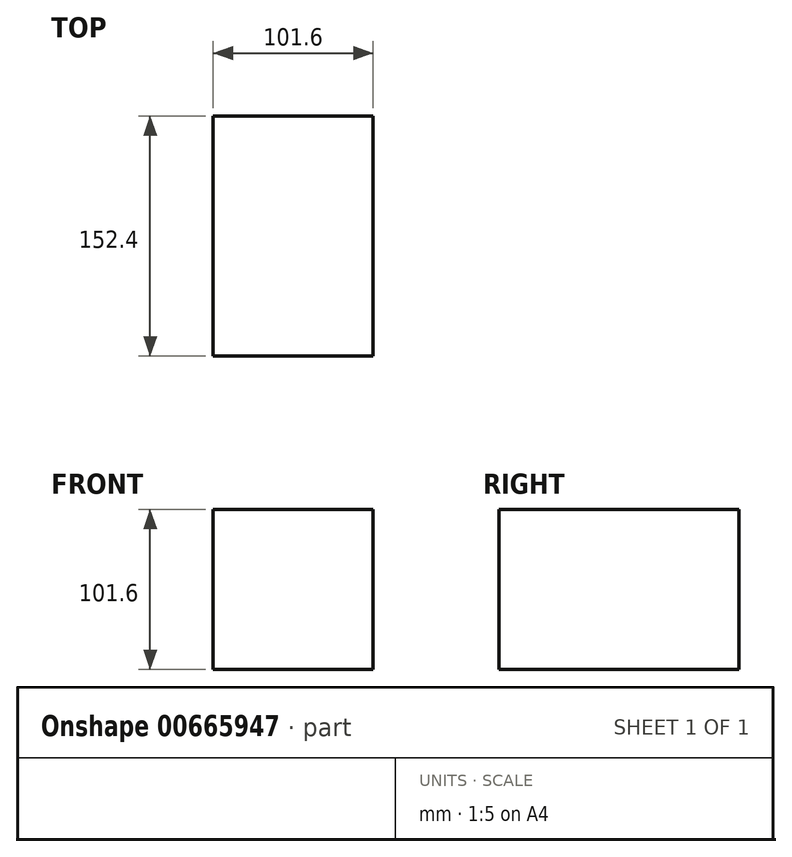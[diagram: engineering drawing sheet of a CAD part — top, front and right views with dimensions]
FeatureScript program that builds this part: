
annotation { "Feature Type Name" : "Feature", "Feature Type Description" : "" }
export const myFeature = defineFeature(function(context is Context, id is Id, definition is map)
    precondition{}
    {
        {
            var Q0;
            Q0=qCreatedBy(makeId("Top.planeOp"),FACE);
            var sketch = newSketch(context, id + "F0", { "sketchPlane" : qUnion([Q0])});
            skLineSegment(sketch, "E0", {"start": v(0, 0) * mm, "end": v(0, 152.4) * mm});
            skLineSegment(sketch, "E1", {"start": v(0, 152.4) * mm, "end": v(101.6, 152.4) * mm});
            skLineSegment(sketch, "E2", {"start": v(101.6, 152.4) * mm, "end": v(101.6, 0) * mm});
            skLineSegment(sketch, "E3", {"start": v(101.6, 0) * mm, "end": v(0, 0) * mm});
            skSolve(sketch);
        }
        {
            var Q0;
            Q0 = qSketchRegion(id + "F0", true);
            extrude(context, id + "F1", {"entities" : qUnion([Q0]), "depth" : 101.6 * mm, "offsetDistance" : 25.4 * mm});
        }
    });
